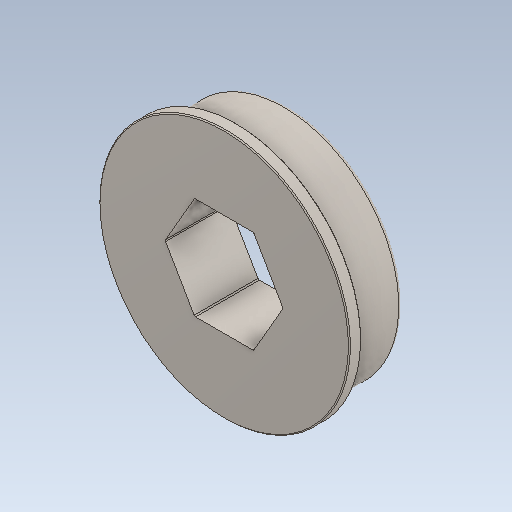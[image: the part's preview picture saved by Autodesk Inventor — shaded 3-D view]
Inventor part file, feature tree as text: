
AUTODESK INVENTOR PART (.ipt)
format: ipt  version: 2023 (Build 270158000, 158)  size: 166,400 bytes
history: native  units: in
note: dims shown in document units (in); Inventor stores cm internally (conversion verified against a paired STEP export)
features: fillet x1
ambient origin geometry x8: Origin, YZ Plane, XZ Plane, XY Plane, X Axis, Y Axis, Z Axis, Center Point
bodies: Solid1 (feature_tree)
feature tree (1):
  fillet  "Fillet2"  [1 undecoded]
note: 1 required parameter value undecoded (feature->parameter linkage not recoverable at this tier; creation-order binding heuristic only, values carry confidence <= 0.55)
